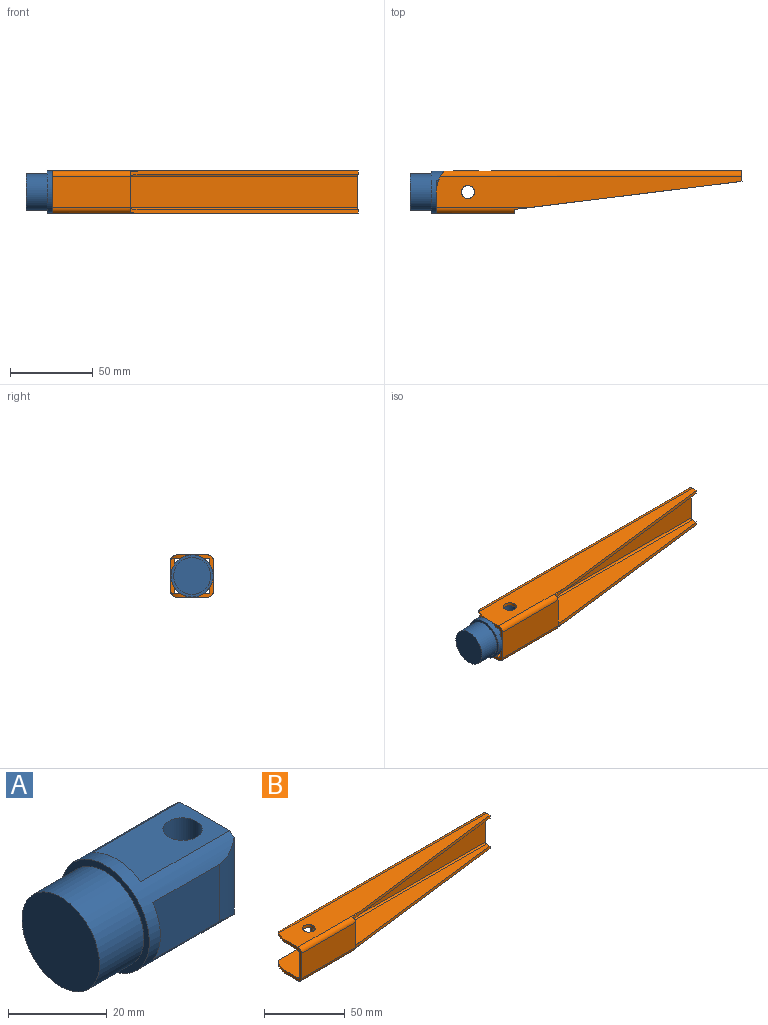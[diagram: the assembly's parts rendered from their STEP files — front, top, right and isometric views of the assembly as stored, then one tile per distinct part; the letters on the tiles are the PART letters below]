
ASSEMBLY  parts=2 mates=1
PART A: 13 faces, bbox 41.3x25.4x25.4 mm
  f0: cylinder r=12.7mm len=28.58mm, axis (-1,0,0), area 1121.1mm2, adj f1,f2,f5,f6,f7,f8,f9,f10
  f1: plane 21.11x21.08mm, normal (1,0,0), area 408.7mm2, adj f0,f6,f10,f12
  f2: plane 25.4x25.4mm, normal (-1,0,0), area 118.8mm2, adj f0,f3
  f3: cylinder r=11.11mm len=22.23mm, axis (1,0,0), area 886.7mm2, adj f2,f4
  f4: plane 22.23x22.23mm, normal (-1,0,0), area 387.9mm2, adj f3
  f5: plane 14.17x2.16mm, normal (1,0,0), area 20.8mm2, adj f0,f6
  f6: plane 25.4x14.17mm, normal (0,0,-1), area 310.4mm2, adj f0,f1,f5,f11
  f7: plane 14.17x2.16mm, normal (1,0,0), area 20.8mm2, adj f0,f8
  f8: plane 19.05x14.17mm, normal (0,-1,0), area 269.9mm2, adj f0,f7,f12
  f9: plane 14.17x2.16mm, normal (1,0,0), area 20.8mm2, adj f0,f10
  f10: plane 25.4x14.17mm, normal (0,0,1), area 310.4mm2, adj f0,f1,f9,f11
  f11: cylinder r=3.97mm len=21.08mm, axis (0,0,1), area 525.7mm2, adj f6,f10
  f12: cylinder r=10.54mm len=19.03mm, axis (0,0,1), area 108.9mm2, adj f0,f1,f8
PART B: 26 faces, bbox 184.3x25.5x25.5 mm
  f0: plane 184.15x19.05mm, normal (0,0,1), area 2424.5mm2, adj f2,f3,f11,f17,f20,f22,f24
  f1: cylinder r=3.17mm len=181.6mm, axis (-1,0,0), area 867.7mm2, adj f4,f6,f7,f17,f18,f21
  f2: plane 25.4x12.7mm, normal (-1,0,0), area 94.4mm2, adj f0,f4,f5,f6,f11,f12,f13,f14
  f3: cylinder r=3.17mm len=181.6mm, axis (-1,0,0), area 867.7mm2, adj f0,f5,f7,f17,f18,f22
  f4: plane 184.15x19.05mm, normal (0,0,-1), area 2424.5mm2, adj f1,f2,f13,f17,f19,f21,f25
  f5: plane 184.15x22.04mm, normal (0,0,-1), area 2513.5mm2, adj f2,f3,f8,f16,f17,f18,f20,f22
  f6: plane 184.15x22.04mm, normal (0,0,1), area 2513.5mm2, adj f1,f2,f10,f14,f17,f18,f19,f21
  f7: plane 150.81x19.05mm, normal (0,1,0), area 2873mm2, adj f1,f3,f17,f18
  f8: cylinder r=1.07mm len=150.81mm, axis (-1,0,0), area 252.7mm2, adj f5,f9,f17,f18
  f9: plane 150.81x19.05mm, normal (0,-1,0), area 2873mm2, adj f8,f10,f17,f18
  f10: cylinder r=1.07mm len=150.81mm, axis (-1,0,0), area 252.7mm2, adj f6,f9,f17,f18
  f11: cylinder r=3.17mm len=54.86mm, axis (-1,0,0), area 239.1mm2, adj f0,f2,f12,f23,f24
  f12: plane 47.34x19.05mm, normal (0,-1,0), area 901.8mm2, adj f2,f11,f13,f23
  f13: cylinder r=3.17mm len=54.86mm, axis (-1,0,0), area 239.1mm2, adj f2,f4,f12,f23,f25
  f14: cylinder r=1.07mm len=54.86mm, axis (-1,0,0), area 83mm2, adj f2,f6,f15,f23,f25
  f15: plane 47.08x19.05mm, normal (0,1,0), area 896.9mm2, adj f2,f14,f16,f23
  f16: cylinder r=1.07mm len=54.86mm, axis (-1,0,0), area 83mm2, adj f2,f5,f15,f23,f24
  f17: plane 25.4x6.35mm, normal (1,0,0), area 67.6mm2, adj f0,f1,f3,f4,f5,f6,f7,f8
  f18: plane 21.18x3.18mm, normal (-1,0,0), area 45mm2, adj f1,f3,f5,f6,f7,f8,f9,f10
  f19: cylinder r=3.97mm len=7.94mm, axis (0,0,1), area 52.6mm2, adj f4,f6
  f20: cylinder r=3.97mm len=7.94mm, axis (0,0,1), area 52.6mm2, adj f0,f5
  f21: cylinder r=19.05mm len=12.52mm, axis (0,0,1), area 26.6mm2, adj f1,f2,f4,f6
  f22: cylinder r=19.05mm len=12.52mm, axis (0,0,1), area 26.6mm2, adj f0,f2,f3,f5
  f23: plane 25.23x2.34mm, normal (0.99,0.12,0), area 50.3mm2, adj f11,f12,f13,f14,f15,f16,f24,f25
  f24: plane 137.18x16.93mm, normal (0.12,-0.99,0), area 292.1mm2, adj f0,f5,f11,f16,f17,f23
  f25: plane 137.18x16.93mm, normal (0.12,-0.99,0), area 292.1mm2, adj f4,f6,f13,f14,f17,f23
PLACE A t=(22.26,24.05,0.42)mm
PLACE B rot(axis=(0,0,1),0deg) t=(25.43,24.04,0.37)mm
MATE cylindrical A.f11 <-> B.f21  axis (0,0,1) through (44.48,24.05,10.96)mm
